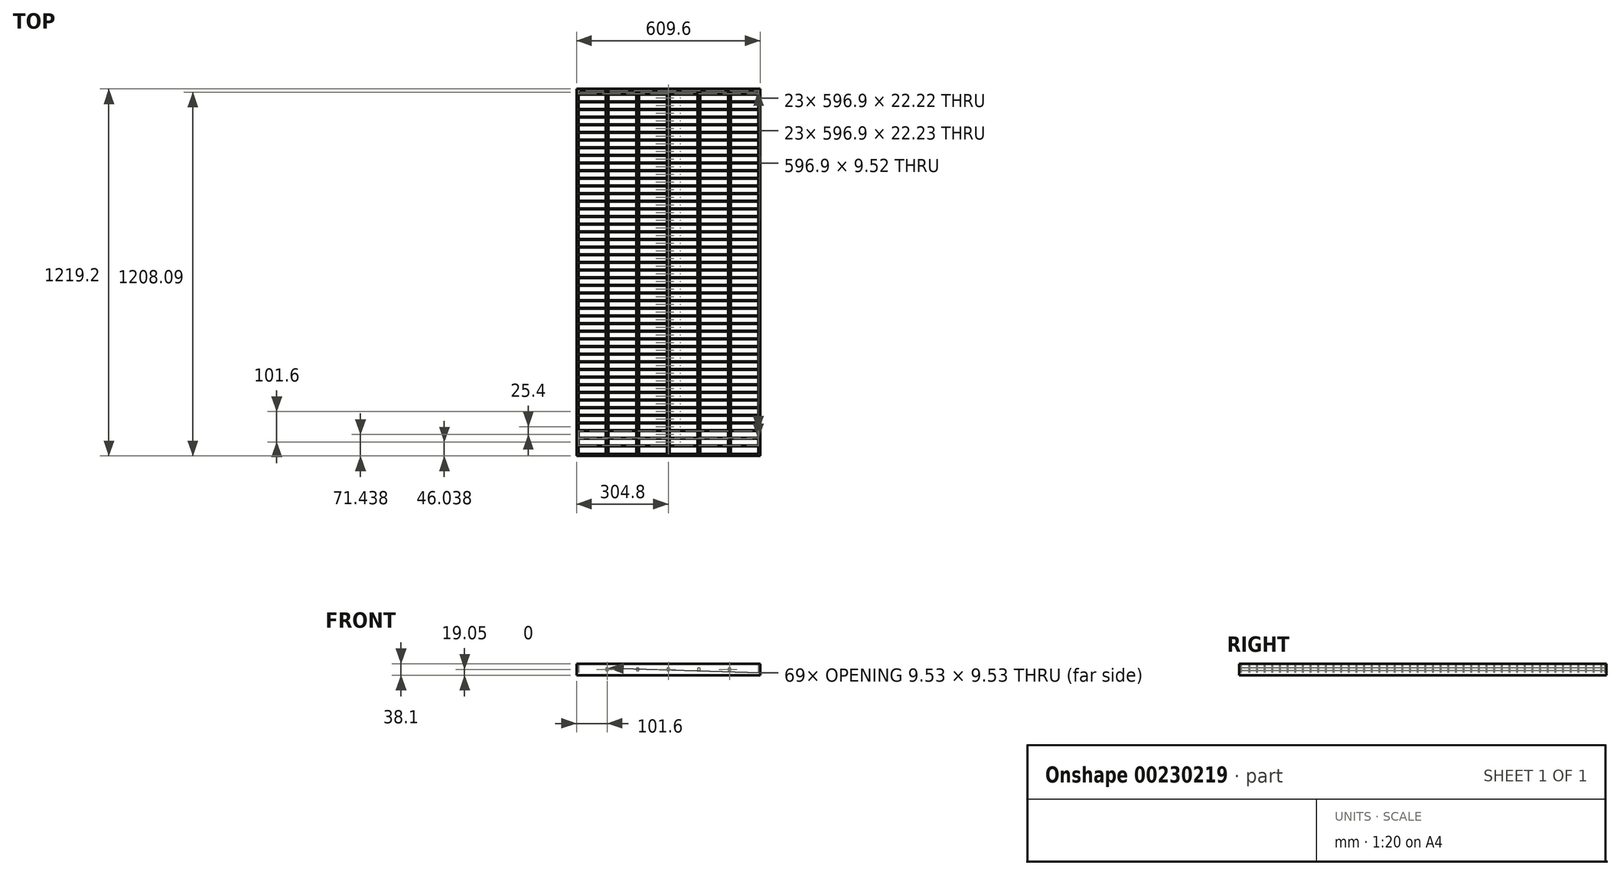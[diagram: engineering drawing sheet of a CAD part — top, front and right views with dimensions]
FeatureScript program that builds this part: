
annotation { "Feature Type Name" : "Feature", "Feature Type Description" : "" }
export const myFeature = defineFeature(function(context is Context, id is Id, definition is map)
    precondition{}
    {
        {
            var Q0;
            Q0=qCreatedBy(makeId("Top.planeOp"),FACE);
            var sketch = newSketch(context, id + "F0", { "sketchPlane" : qUnion([Q0])});
            skLineSegment(sketch, "E0.bottom", {"start": v(304.8, 609.6) * mm, "end": v(-304.8, 609.6) * mm});
            skLineSegment(sketch, "E0.top", {"start": v(304.8, -609.6) * mm, "end": v(-304.8, -609.6) * mm});
            skLineSegment(sketch, "E0.left", {"start": v(304.8, 609.6) * mm, "end": v(304.8, -609.6) * mm});
            skLineSegment(sketch, "E0.right", {"start": v(-304.8, 609.6) * mm, "end": v(-304.8, -609.6) * mm});
            skPoint(sketch, "E0.middle", {"position": v(0, 0) * mm});
            skLineSegment(sketch, "E1.bottom", {"start": v(-298.45, 603.25) * mm, "end": v(298.45, 603.25) * mm});
            skLineSegment(sketch, "E1.top", {"start": v(-298.45, -603.25) * mm, "end": v(298.45, -603.25) * mm});
            skLineSegment(sketch, "E1.left", {"start": v(-298.45, 603.25) * mm, "end": v(-298.45, -603.25) * mm});
            skLineSegment(sketch, "E1.right", {"start": v(298.45, 603.25) * mm, "end": v(298.45, -603.25) * mm});
            skLineSegment(sketch, "E2", {"start": v(-298.45, -603.25) * mm, "end": v(-298.45, -577.85) * mm});
            skLineSegment(sketch, "E3", {"start": v(-298.45, -577.85) * mm, "end": v(298.45, -577.85) * mm});
            skLineSegment(sketch, "E4", {"start": v(298.45, -577.85) * mm, "end": v(298.45, -574.67) * mm});
            skLineSegment(sketch, "E5", {"start": v(298.45, -574.67) * mm, "end": v(-298.45, -574.67) * mm});
            skLineSegment(sketch, "E6", {"start": v(-298.45, -574.67) * mm, "end": v(-298.45, -577.85) * mm});
            skLineSegment(sketch, "E7.0.1.0", {"start": v(-298.45, -552.45) * mm, "end": v(298.45, -552.45) * mm});
            skLineSegment(sketch, "E7.0.1.1", {"start": v(298.45, -549.27) * mm, "end": v(-298.45, -549.27) * mm});
            skLineSegment(sketch, "E7.0.1.2", {"start": v(298.45, -552.45) * mm, "end": v(298.45, -549.27) * mm});
            skLineSegment(sketch, "E7.0.1.3", {"start": v(-298.45, -549.27) * mm, "end": v(-298.45, -552.45) * mm});
            skLineSegment(sketch, "E7.0.2.0", {"start": v(-298.45, -527.05) * mm, "end": v(298.45, -527.05) * mm});
            skLineSegment(sketch, "E7.0.2.1", {"start": v(298.45, -523.88) * mm, "end": v(-298.45, -523.88) * mm});
            skLineSegment(sketch, "E7.0.2.2", {"start": v(298.45, -527.05) * mm, "end": v(298.45, -523.88) * mm});
            skLineSegment(sketch, "E7.0.2.3", {"start": v(-298.45, -523.88) * mm, "end": v(-298.45, -527.05) * mm});
            skLineSegment(sketch, "E7.0.3.0", {"start": v(-298.45, -501.65) * mm, "end": v(298.45, -501.65) * mm});
            skLineSegment(sketch, "E7.0.3.1", {"start": v(298.45, -498.48) * mm, "end": v(-298.45, -498.47) * mm});
            skLineSegment(sketch, "E7.0.3.2", {"start": v(298.45, -501.65) * mm, "end": v(298.45, -498.48) * mm});
            skLineSegment(sketch, "E7.0.3.3", {"start": v(-298.45, -498.48) * mm, "end": v(-298.45, -501.65) * mm});
            skLineSegment(sketch, "E7.0.4.0", {"start": v(-298.45, -476.25) * mm, "end": v(298.45, -476.25) * mm});
            skLineSegment(sketch, "E7.0.4.1", {"start": v(298.45, -473.08) * mm, "end": v(-298.45, -473.07) * mm});
            skLineSegment(sketch, "E7.0.4.2", {"start": v(298.45, -476.25) * mm, "end": v(298.45, -473.08) * mm});
            skLineSegment(sketch, "E7.0.4.3", {"start": v(-298.45, -473.08) * mm, "end": v(-298.45, -476.25) * mm});
            skLineSegment(sketch, "E7.0.5.0", {"start": v(-298.45, -450.85) * mm, "end": v(298.45, -450.85) * mm});
            skLineSegment(sketch, "E7.0.5.1", {"start": v(298.45, -447.68) * mm, "end": v(-298.45, -447.68) * mm});
            skLineSegment(sketch, "E7.0.5.2", {"start": v(298.45, -450.85) * mm, "end": v(298.45, -447.68) * mm});
            skLineSegment(sketch, "E7.0.5.3", {"start": v(-298.45, -447.68) * mm, "end": v(-298.45, -450.85) * mm});
            skLineSegment(sketch, "E7.0.6.0", {"start": v(-298.45, -425.45) * mm, "end": v(298.45, -425.45) * mm});
            skLineSegment(sketch, "E7.0.6.1", {"start": v(298.45, -422.28) * mm, "end": v(-298.45, -422.28) * mm});
            skLineSegment(sketch, "E7.0.6.2", {"start": v(298.45, -425.45) * mm, "end": v(298.45, -422.28) * mm});
            skLineSegment(sketch, "E7.0.6.3", {"start": v(-298.45, -422.28) * mm, "end": v(-298.45, -425.45) * mm});
            skLineSegment(sketch, "E7.0.7.0", {"start": v(-298.45, -400.05) * mm, "end": v(298.45, -400.05) * mm});
            skLineSegment(sketch, "E7.0.7.1", {"start": v(298.45, -396.88) * mm, "end": v(-298.45, -396.88) * mm});
            skLineSegment(sketch, "E7.0.7.2", {"start": v(298.45, -400.05) * mm, "end": v(298.45, -396.88) * mm});
            skLineSegment(sketch, "E7.0.7.3", {"start": v(-298.45, -396.88) * mm, "end": v(-298.45, -400.05) * mm});
            skLineSegment(sketch, "E7.0.8.0", {"start": v(-298.45, -374.65) * mm, "end": v(298.45, -374.65) * mm});
            skLineSegment(sketch, "E7.0.8.1", {"start": v(298.45, -371.48) * mm, "end": v(-298.45, -371.48) * mm});
            skLineSegment(sketch, "E7.0.8.2", {"start": v(298.45, -374.65) * mm, "end": v(298.45, -371.48) * mm});
            skLineSegment(sketch, "E7.0.8.3", {"start": v(-298.45, -371.48) * mm, "end": v(-298.45, -374.65) * mm});
            skLineSegment(sketch, "E7.0.9.0", {"start": v(-298.45, -349.25) * mm, "end": v(298.45, -349.25) * mm});
            skLineSegment(sketch, "E7.0.9.1", {"start": v(298.45, -346.08) * mm, "end": v(-298.45, -346.08) * mm});
            skLineSegment(sketch, "E7.0.9.2", {"start": v(298.45, -349.25) * mm, "end": v(298.45, -346.08) * mm});
            skLineSegment(sketch, "E7.0.9.3", {"start": v(-298.45, -346.08) * mm, "end": v(-298.45, -349.25) * mm});
            skLineSegment(sketch, "E7.0.10.0", {"start": v(-298.45, -323.85) * mm, "end": v(298.45, -323.85) * mm});
            skLineSegment(sketch, "E7.0.10.1", {"start": v(298.45, -320.68) * mm, "end": v(-298.45, -320.68) * mm});
            skLineSegment(sketch, "E7.0.10.2", {"start": v(298.45, -323.85) * mm, "end": v(298.45, -320.68) * mm});
            skLineSegment(sketch, "E7.0.10.3", {"start": v(-298.45, -320.68) * mm, "end": v(-298.45, -323.85) * mm});
            skLineSegment(sketch, "E7.0.11.0", {"start": v(-298.45, -298.45) * mm, "end": v(298.45, -298.45) * mm});
            skLineSegment(sketch, "E7.0.11.1", {"start": v(298.45, -295.28) * mm, "end": v(-298.45, -295.28) * mm});
            skLineSegment(sketch, "E7.0.11.2", {"start": v(298.45, -298.45) * mm, "end": v(298.45, -295.28) * mm});
            skLineSegment(sketch, "E7.0.11.3", {"start": v(-298.45, -295.28) * mm, "end": v(-298.45, -298.45) * mm});
            skLineSegment(sketch, "E7.0.12.0", {"start": v(-298.45, -273.05) * mm, "end": v(298.45, -273.05) * mm});
            skLineSegment(sketch, "E7.0.12.1", {"start": v(298.45, -269.88) * mm, "end": v(-298.45, -269.88) * mm});
            skLineSegment(sketch, "E7.0.12.2", {"start": v(298.45, -273.05) * mm, "end": v(298.45, -269.88) * mm});
            skLineSegment(sketch, "E7.0.12.3", {"start": v(-298.45, -269.88) * mm, "end": v(-298.45, -273.05) * mm});
            skLineSegment(sketch, "E7.0.13.0", {"start": v(-298.45, -247.65) * mm, "end": v(298.45, -247.65) * mm});
            skLineSegment(sketch, "E7.0.13.1", {"start": v(298.45, -244.48) * mm, "end": v(-298.45, -244.48) * mm});
            skLineSegment(sketch, "E7.0.13.2", {"start": v(298.45, -247.65) * mm, "end": v(298.45, -244.48) * mm});
            skLineSegment(sketch, "E7.0.13.3", {"start": v(-298.45, -244.48) * mm, "end": v(-298.45, -247.65) * mm});
            skLineSegment(sketch, "E7.0.14.0", {"start": v(-298.45, -222.25) * mm, "end": v(298.45, -222.25) * mm});
            skLineSegment(sketch, "E7.0.14.1", {"start": v(298.45, -219.08) * mm, "end": v(-298.45, -219.08) * mm});
            skLineSegment(sketch, "E7.0.14.2", {"start": v(298.45, -222.25) * mm, "end": v(298.45, -219.08) * mm});
            skLineSegment(sketch, "E7.0.14.3", {"start": v(-298.45, -219.08) * mm, "end": v(-298.45, -222.25) * mm});
            skLineSegment(sketch, "E7.0.15.0", {"start": v(-298.45, -196.85) * mm, "end": v(298.45, -196.85) * mm});
            skLineSegment(sketch, "E7.0.15.1", {"start": v(298.45, -193.68) * mm, "end": v(-298.45, -193.68) * mm});
            skLineSegment(sketch, "E7.0.15.2", {"start": v(298.45, -196.85) * mm, "end": v(298.45, -193.68) * mm});
            skLineSegment(sketch, "E7.0.15.3", {"start": v(-298.45, -193.68) * mm, "end": v(-298.45, -196.85) * mm});
            skLineSegment(sketch, "E7.0.16.0", {"start": v(-298.45, -171.45) * mm, "end": v(298.45, -171.45) * mm});
            skLineSegment(sketch, "E7.0.16.1", {"start": v(298.45, -168.28) * mm, "end": v(-298.45, -168.28) * mm});
            skLineSegment(sketch, "E7.0.16.2", {"start": v(298.45, -171.45) * mm, "end": v(298.45, -168.28) * mm});
            skLineSegment(sketch, "E7.0.16.3", {"start": v(-298.45, -168.28) * mm, "end": v(-298.45, -171.45) * mm});
            skLineSegment(sketch, "E7.0.17.0", {"start": v(-298.45, -146.05) * mm, "end": v(298.45, -146.05) * mm});
            skLineSegment(sketch, "E7.0.17.1", {"start": v(298.45, -142.88) * mm, "end": v(-298.45, -142.88) * mm});
            skLineSegment(sketch, "E7.0.17.2", {"start": v(298.45, -146.05) * mm, "end": v(298.45, -142.88) * mm});
            skLineSegment(sketch, "E7.0.17.3", {"start": v(-298.45, -142.88) * mm, "end": v(-298.45, -146.05) * mm});
            skLineSegment(sketch, "E7.0.18.0", {"start": v(-298.45, -120.65) * mm, "end": v(298.45, -120.65) * mm});
            skLineSegment(sketch, "E7.0.18.1", {"start": v(298.45, -117.48) * mm, "end": v(-298.45, -117.48) * mm});
            skLineSegment(sketch, "E7.0.18.2", {"start": v(298.45, -120.65) * mm, "end": v(298.45, -117.48) * mm});
            skLineSegment(sketch, "E7.0.18.3", {"start": v(-298.45, -117.48) * mm, "end": v(-298.45, -120.65) * mm});
            skLineSegment(sketch, "E7.0.19.0", {"start": v(-298.45, -95.25) * mm, "end": v(298.45, -95.25) * mm});
            skLineSegment(sketch, "E7.0.19.1", {"start": v(298.45, -92.08) * mm, "end": v(-298.45, -92.08) * mm});
            skLineSegment(sketch, "E7.0.19.2", {"start": v(298.45, -95.25) * mm, "end": v(298.45, -92.08) * mm});
            skLineSegment(sketch, "E7.0.19.3", {"start": v(-298.45, -92.08) * mm, "end": v(-298.45, -95.25) * mm});
            skLineSegment(sketch, "E7.0.20.0", {"start": v(-298.45, -69.85) * mm, "end": v(298.45, -69.85) * mm});
            skLineSegment(sketch, "E7.0.20.1", {"start": v(298.45, -66.68) * mm, "end": v(-298.45, -66.68) * mm});
            skLineSegment(sketch, "E7.0.20.2", {"start": v(298.45, -69.85) * mm, "end": v(298.45, -66.68) * mm});
            skLineSegment(sketch, "E7.0.20.3", {"start": v(-298.45, -66.68) * mm, "end": v(-298.45, -69.85) * mm});
            skLineSegment(sketch, "E7.0.21.0", {"start": v(-298.45, -44.45) * mm, "end": v(298.45, -44.45) * mm});
            skLineSegment(sketch, "E7.0.21.1", {"start": v(298.45, -41.28) * mm, "end": v(-298.45, -41.28) * mm});
            skLineSegment(sketch, "E7.0.21.2", {"start": v(298.45, -44.45) * mm, "end": v(298.45, -41.28) * mm});
            skLineSegment(sketch, "E7.0.21.3", {"start": v(-298.45, -41.28) * mm, "end": v(-298.45, -44.45) * mm});
            skLineSegment(sketch, "E7.0.22.0", {"start": v(-298.45, -19.05) * mm, "end": v(298.45, -19.05) * mm});
            skLineSegment(sketch, "E7.0.22.1", {"start": v(298.45, -15.88) * mm, "end": v(-298.45, -15.88) * mm});
            skLineSegment(sketch, "E7.0.22.2", {"start": v(298.45, -19.05) * mm, "end": v(298.45, -15.88) * mm});
            skLineSegment(sketch, "E7.0.22.3", {"start": v(-298.45, -15.88) * mm, "end": v(-298.45, -19.05) * mm});
            skLineSegment(sketch, "E7.0.23.0", {"start": v(-298.45, 6.35) * mm, "end": v(298.45, 6.35) * mm});
            skLineSegment(sketch, "E7.0.23.1", {"start": v(298.45, 9.52) * mm, "end": v(-298.45, 9.52) * mm});
            skLineSegment(sketch, "E7.0.23.2", {"start": v(298.45, 6.35) * mm, "end": v(298.45, 9.52) * mm});
            skLineSegment(sketch, "E7.0.23.3", {"start": v(-298.45, 9.52) * mm, "end": v(-298.45, 6.35) * mm});
            skLineSegment(sketch, "E7.0.24.0", {"start": v(-298.45, 31.75) * mm, "end": v(298.45, 31.75) * mm});
            skLineSegment(sketch, "E7.0.24.1", {"start": v(298.45, 34.92) * mm, "end": v(-298.45, 34.92) * mm});
            skLineSegment(sketch, "E7.0.24.2", {"start": v(298.45, 31.75) * mm, "end": v(298.45, 34.92) * mm});
            skLineSegment(sketch, "E7.0.24.3", {"start": v(-298.45, 34.92) * mm, "end": v(-298.45, 31.75) * mm});
            skLineSegment(sketch, "E7.0.25.0", {"start": v(-298.45, 57.15) * mm, "end": v(298.45, 57.15) * mm});
            skLineSegment(sketch, "E7.0.25.1", {"start": v(298.45, 60.32) * mm, "end": v(-298.45, 60.32) * mm});
            skLineSegment(sketch, "E7.0.25.2", {"start": v(298.45, 57.15) * mm, "end": v(298.45, 60.32) * mm});
            skLineSegment(sketch, "E7.0.25.3", {"start": v(-298.45, 60.32) * mm, "end": v(-298.45, 57.15) * mm});
            skLineSegment(sketch, "E7.0.26.0", {"start": v(-298.45, 82.55) * mm, "end": v(298.45, 82.55) * mm});
            skLineSegment(sketch, "E7.0.26.1", {"start": v(298.45, 85.72) * mm, "end": v(-298.45, 85.72) * mm});
            skLineSegment(sketch, "E7.0.26.2", {"start": v(298.45, 82.55) * mm, "end": v(298.45, 85.72) * mm});
            skLineSegment(sketch, "E7.0.26.3", {"start": v(-298.45, 85.72) * mm, "end": v(-298.45, 82.55) * mm});
            skLineSegment(sketch, "E7.0.27.0", {"start": v(-298.45, 107.95) * mm, "end": v(298.45, 107.95) * mm});
            skLineSegment(sketch, "E7.0.27.1", {"start": v(298.45, 111.12) * mm, "end": v(-298.45, 111.12) * mm});
            skLineSegment(sketch, "E7.0.27.2", {"start": v(298.45, 107.95) * mm, "end": v(298.45, 111.12) * mm});
            skLineSegment(sketch, "E7.0.27.3", {"start": v(-298.45, 111.12) * mm, "end": v(-298.45, 107.95) * mm});
            skLineSegment(sketch, "E7.0.28.0", {"start": v(-298.45, 133.35) * mm, "end": v(298.45, 133.35) * mm});
            skLineSegment(sketch, "E7.0.28.1", {"start": v(298.45, 136.52) * mm, "end": v(-298.45, 136.52) * mm});
            skLineSegment(sketch, "E7.0.28.2", {"start": v(298.45, 133.35) * mm, "end": v(298.45, 136.52) * mm});
            skLineSegment(sketch, "E7.0.28.3", {"start": v(-298.45, 136.52) * mm, "end": v(-298.45, 133.35) * mm});
            skLineSegment(sketch, "E7.0.29.0", {"start": v(-298.45, 158.75) * mm, "end": v(298.45, 158.75) * mm});
            skLineSegment(sketch, "E7.0.29.1", {"start": v(298.45, 161.92) * mm, "end": v(-298.45, 161.92) * mm});
            skLineSegment(sketch, "E7.0.29.2", {"start": v(298.45, 158.75) * mm, "end": v(298.45, 161.92) * mm});
            skLineSegment(sketch, "E7.0.29.3", {"start": v(-298.45, 161.92) * mm, "end": v(-298.45, 158.75) * mm});
            skLineSegment(sketch, "E7.0.30.0", {"start": v(-298.45, 184.15) * mm, "end": v(298.45, 184.15) * mm});
            skLineSegment(sketch, "E7.0.30.1", {"start": v(298.45, 187.32) * mm, "end": v(-298.45, 187.32) * mm});
            skLineSegment(sketch, "E7.0.30.2", {"start": v(298.45, 184.15) * mm, "end": v(298.45, 187.32) * mm});
            skLineSegment(sketch, "E7.0.30.3", {"start": v(-298.45, 187.32) * mm, "end": v(-298.45, 184.15) * mm});
            skLineSegment(sketch, "E7.0.31.0", {"start": v(-298.45, 209.55) * mm, "end": v(298.45, 209.55) * mm});
            skLineSegment(sketch, "E7.0.31.1", {"start": v(298.45, 212.72) * mm, "end": v(-298.45, 212.72) * mm});
            skLineSegment(sketch, "E7.0.31.2", {"start": v(298.45, 209.55) * mm, "end": v(298.45, 212.72) * mm});
            skLineSegment(sketch, "E7.0.31.3", {"start": v(-298.45, 212.72) * mm, "end": v(-298.45, 209.55) * mm});
            skLineSegment(sketch, "E7.0.32.0", {"start": v(-298.45, 234.95) * mm, "end": v(298.45, 234.95) * mm});
            skLineSegment(sketch, "E7.0.32.1", {"start": v(298.45, 238.12) * mm, "end": v(-298.45, 238.12) * mm});
            skLineSegment(sketch, "E7.0.32.2", {"start": v(298.45, 234.95) * mm, "end": v(298.45, 238.12) * mm});
            skLineSegment(sketch, "E7.0.32.3", {"start": v(-298.45, 238.12) * mm, "end": v(-298.45, 234.95) * mm});
            skLineSegment(sketch, "E7.0.33.0", {"start": v(-298.45, 260.35) * mm, "end": v(298.45, 260.35) * mm});
            skLineSegment(sketch, "E7.0.33.1", {"start": v(298.45, 263.52) * mm, "end": v(-298.45, 263.52) * mm});
            skLineSegment(sketch, "E7.0.33.2", {"start": v(298.45, 260.35) * mm, "end": v(298.45, 263.52) * mm});
            skLineSegment(sketch, "E7.0.33.3", {"start": v(-298.45, 263.52) * mm, "end": v(-298.45, 260.35) * mm});
            skLineSegment(sketch, "E7.0.34.0", {"start": v(-298.45, 285.75) * mm, "end": v(298.45, 285.75) * mm});
            skLineSegment(sketch, "E7.0.34.1", {"start": v(298.45, 288.92) * mm, "end": v(-298.45, 288.92) * mm});
            skLineSegment(sketch, "E7.0.34.2", {"start": v(298.45, 285.75) * mm, "end": v(298.45, 288.92) * mm});
            skLineSegment(sketch, "E7.0.34.3", {"start": v(-298.45, 288.92) * mm, "end": v(-298.45, 285.75) * mm});
            skLineSegment(sketch, "E7.0.35.0", {"start": v(-298.45, 311.15) * mm, "end": v(298.45, 311.15) * mm});
            skLineSegment(sketch, "E7.0.35.1", {"start": v(298.45, 314.32) * mm, "end": v(-298.45, 314.32) * mm});
            skLineSegment(sketch, "E7.0.35.2", {"start": v(298.45, 311.15) * mm, "end": v(298.45, 314.32) * mm});
            skLineSegment(sketch, "E7.0.35.3", {"start": v(-298.45, 314.32) * mm, "end": v(-298.45, 311.15) * mm});
            skLineSegment(sketch, "E7.0.36.0", {"start": v(-298.45, 336.55) * mm, "end": v(298.45, 336.55) * mm});
            skLineSegment(sketch, "E7.0.36.1", {"start": v(298.45, 339.72) * mm, "end": v(-298.45, 339.72) * mm});
            skLineSegment(sketch, "E7.0.36.2", {"start": v(298.45, 336.55) * mm, "end": v(298.45, 339.72) * mm});
            skLineSegment(sketch, "E7.0.36.3", {"start": v(-298.45, 339.72) * mm, "end": v(-298.45, 336.55) * mm});
            skLineSegment(sketch, "E7.0.37.0", {"start": v(-298.45, 361.95) * mm, "end": v(298.45, 361.95) * mm});
            skLineSegment(sketch, "E7.0.37.1", {"start": v(298.45, 365.12) * mm, "end": v(-298.45, 365.12) * mm});
            skLineSegment(sketch, "E7.0.37.2", {"start": v(298.45, 361.95) * mm, "end": v(298.45, 365.12) * mm});
            skLineSegment(sketch, "E7.0.37.3", {"start": v(-298.45, 365.12) * mm, "end": v(-298.45, 361.95) * mm});
            skLineSegment(sketch, "E7.0.38.0", {"start": v(-298.45, 387.35) * mm, "end": v(298.45, 387.35) * mm});
            skLineSegment(sketch, "E7.0.38.1", {"start": v(298.45, 390.52) * mm, "end": v(-298.45, 390.52) * mm});
            skLineSegment(sketch, "E7.0.38.2", {"start": v(298.45, 387.35) * mm, "end": v(298.45, 390.52) * mm});
            skLineSegment(sketch, "E7.0.38.3", {"start": v(-298.45, 390.52) * mm, "end": v(-298.45, 387.35) * mm});
            skLineSegment(sketch, "E7.0.39.0", {"start": v(-298.45, 412.75) * mm, "end": v(298.45, 412.75) * mm});
            skLineSegment(sketch, "E7.0.39.1", {"start": v(298.45, 415.92) * mm, "end": v(-298.45, 415.92) * mm});
            skLineSegment(sketch, "E7.0.39.2", {"start": v(298.45, 412.75) * mm, "end": v(298.45, 415.92) * mm});
            skLineSegment(sketch, "E7.0.39.3", {"start": v(-298.45, 415.92) * mm, "end": v(-298.45, 412.75) * mm});
            skLineSegment(sketch, "E7.0.40.0", {"start": v(-298.45, 438.15) * mm, "end": v(298.45, 438.15) * mm});
            skLineSegment(sketch, "E7.0.40.1", {"start": v(298.45, 441.32) * mm, "end": v(-298.45, 441.32) * mm});
            skLineSegment(sketch, "E7.0.40.2", {"start": v(298.45, 438.15) * mm, "end": v(298.45, 441.32) * mm});
            skLineSegment(sketch, "E7.0.40.3", {"start": v(-298.45, 441.32) * mm, "end": v(-298.45, 438.15) * mm});
            skLineSegment(sketch, "E7.0.41.0", {"start": v(-298.45, 463.55) * mm, "end": v(298.45, 463.55) * mm});
            skLineSegment(sketch, "E7.0.41.1", {"start": v(298.45, 466.72) * mm, "end": v(-298.45, 466.72) * mm});
            skLineSegment(sketch, "E7.0.41.2", {"start": v(298.45, 463.55) * mm, "end": v(298.45, 466.72) * mm});
            skLineSegment(sketch, "E7.0.41.3", {"start": v(-298.45, 466.72) * mm, "end": v(-298.45, 463.55) * mm});
            skLineSegment(sketch, "E7.0.42.0", {"start": v(-298.45, 488.95) * mm, "end": v(298.45, 488.95) * mm});
            skLineSegment(sketch, "E7.0.42.1", {"start": v(298.45, 492.12) * mm, "end": v(-298.45, 492.12) * mm});
            skLineSegment(sketch, "E7.0.42.2", {"start": v(298.45, 488.95) * mm, "end": v(298.45, 492.12) * mm});
            skLineSegment(sketch, "E7.0.42.3", {"start": v(-298.45, 492.12) * mm, "end": v(-298.45, 488.95) * mm});
            skLineSegment(sketch, "E7.0.43.0", {"start": v(-298.45, 514.35) * mm, "end": v(298.45, 514.35) * mm});
            skLineSegment(sketch, "E7.0.43.1", {"start": v(298.45, 517.52) * mm, "end": v(-298.45, 517.52) * mm});
            skLineSegment(sketch, "E7.0.43.2", {"start": v(298.45, 514.35) * mm, "end": v(298.45, 517.52) * mm});
            skLineSegment(sketch, "E7.0.43.3", {"start": v(-298.45, 517.52) * mm, "end": v(-298.45, 514.35) * mm});
            skLineSegment(sketch, "E7.0.44.0", {"start": v(-298.45, 539.75) * mm, "end": v(298.45, 539.75) * mm});
            skLineSegment(sketch, "E7.0.44.1", {"start": v(298.45, 542.92) * mm, "end": v(-298.45, 542.92) * mm});
            skLineSegment(sketch, "E7.0.44.2", {"start": v(298.45, 539.75) * mm, "end": v(298.45, 542.92) * mm});
            skLineSegment(sketch, "E7.0.44.3", {"start": v(-298.45, 542.92) * mm, "end": v(-298.45, 539.75) * mm});
            skLineSegment(sketch, "E7.0.45.0", {"start": v(-298.45, 565.15) * mm, "end": v(298.45, 565.15) * mm});
            skLineSegment(sketch, "E7.0.45.1", {"start": v(298.45, 568.32) * mm, "end": v(-298.45, 568.32) * mm});
            skLineSegment(sketch, "E7.0.45.2", {"start": v(298.45, 565.15) * mm, "end": v(298.45, 568.32) * mm});
            skLineSegment(sketch, "E7.0.45.3", {"start": v(-298.45, 568.32) * mm, "end": v(-298.45, 565.15) * mm});
            skLineSegment(sketch, "E7.0.46.0", {"start": v(-298.45, 590.55) * mm, "end": v(298.45, 590.55) * mm});
            skLineSegment(sketch, "E7.0.46.1", {"start": v(298.45, 593.72) * mm, "end": v(-298.45, 593.72) * mm});
            skLineSegment(sketch, "E7.0.46.2", {"start": v(298.45, 590.55) * mm, "end": v(298.45, 593.72) * mm});
            skLineSegment(sketch, "E7.0.46.3", {"start": v(-298.45, 593.72) * mm, "end": v(-298.45, 590.55) * mm});
            skLineSegment(sketch, "E7.direction1", {"start": v(-298.45, -577.85) * mm, "end": v(-273.05, -577.85) * mm, "construction": true});
            skLineSegment(sketch, "E7.direction2", {"start": v(-298.45, -577.85) * mm, "end": v(-298.45, -552.45) * mm, "construction": true});
            skSolve(sketch);
        }
        {
            var Q0;
            Q0 = qSketchRegion(id + "F0", true);
            var Q1;
            Q1=makeQuery(id+"F0.imprint","IMPRINT",FACE,{"disambiguationData":[TD([[makeQuery(id+"F0.imprint","IMPRINT",EDGE,{"derivedFrom":sQuery(id+"F0.wireOp",EDGE,"E3")}),1.0]])]});
            var Q2;
            Q2=makeQuery(id+"F0.imprint","IMPRINT",FACE,{"disambiguationData":[TD([[makeQuery(id+"F0.imprint","IMPRINT",EDGE,{"derivedFrom":sQuery(id+"F0.wireOp",EDGE,"E7.0.1.0")}),1.0]])]});
            var Q3;
            Q3=makeQuery(id+"F0.imprint","IMPRINT",FACE,{"disambiguationData":[TD([[makeQuery(id+"F0.imprint","IMPRINT",EDGE,{"derivedFrom":sQuery(id+"F0.wireOp",EDGE,"E7.0.2.0")}),1.0]])]});
            var Q4;
            Q4=makeQuery(id+"F0.imprint","IMPRINT",FACE,{"disambiguationData":[TD([[makeQuery(id+"F0.imprint","IMPRINT",EDGE,{"derivedFrom":sQuery(id+"F0.wireOp",EDGE,"E7.0.3.0")}),1.0]])]});
            var Q5;
            Q5=makeQuery(id+"F0.imprint","IMPRINT",FACE,{"disambiguationData":[TD([[makeQuery(id+"F0.imprint","IMPRINT",EDGE,{"derivedFrom":sQuery(id+"F0.wireOp",EDGE,"E7.0.4.0")}),1.0]])]});
            var Q6;
            Q6=makeQuery(id+"F0.imprint","IMPRINT",FACE,{"disambiguationData":[TD([[makeQuery(id+"F0.imprint","IMPRINT",EDGE,{"derivedFrom":sQuery(id+"F0.wireOp",EDGE,"E7.0.5.0")}),1.0]])]});
            var Q7;
            Q7=makeQuery(id+"F0.imprint","IMPRINT",FACE,{"disambiguationData":[TD([[makeQuery(id+"F0.imprint","IMPRINT",EDGE,{"derivedFrom":sQuery(id+"F0.wireOp",EDGE,"E7.0.6.0")}),1.0]])]});
            var Q8;
            Q8=makeQuery(id+"F0.imprint","IMPRINT",FACE,{"disambiguationData":[TD([[makeQuery(id+"F0.imprint","IMPRINT",EDGE,{"derivedFrom":sQuery(id+"F0.wireOp",EDGE,"E7.0.7.0")}),1.0]])]});
            var Q9;
            Q9=makeQuery(id+"F0.imprint","IMPRINT",FACE,{"disambiguationData":[TD([[makeQuery(id+"F0.imprint","IMPRINT",EDGE,{"derivedFrom":sQuery(id+"F0.wireOp",EDGE,"E7.0.8.0")}),1.0]])]});
            var Q10;
            Q10=makeQuery(id+"F0.imprint","IMPRINT",FACE,{"disambiguationData":[TD([[makeQuery(id+"F0.imprint","IMPRINT",EDGE,{"derivedFrom":sQuery(id+"F0.wireOp",EDGE,"E7.0.9.0")}),1.0]])]});
            var Q11;
            Q11=makeQuery(id+"F0.imprint","IMPRINT",FACE,{"disambiguationData":[TD([[makeQuery(id+"F0.imprint","IMPRINT",EDGE,{"derivedFrom":sQuery(id+"F0.wireOp",EDGE,"E7.0.10.0")}),1.0]])]});
            var Q12;
            Q12=makeQuery(id+"F0.imprint","IMPRINT",FACE,{"disambiguationData":[TD([[makeQuery(id+"F0.imprint","IMPRINT",EDGE,{"derivedFrom":sQuery(id+"F0.wireOp",EDGE,"E7.0.11.0")}),1.0]])]});
            var Q13;
            Q13=makeQuery(id+"F0.imprint","IMPRINT",FACE,{"disambiguationData":[TD([[makeQuery(id+"F0.imprint","IMPRINT",EDGE,{"derivedFrom":sQuery(id+"F0.wireOp",EDGE,"E7.0.12.0")}),1.0]])]});
            var Q14;
            Q14=makeQuery(id+"F0.imprint","IMPRINT",FACE,{"disambiguationData":[TD([[makeQuery(id+"F0.imprint","IMPRINT",EDGE,{"derivedFrom":sQuery(id+"F0.wireOp",EDGE,"E7.0.13.0")}),1.0]])]});
            var Q15;
            Q15=makeQuery(id+"F0.imprint","IMPRINT",FACE,{"disambiguationData":[TD([[makeQuery(id+"F0.imprint","IMPRINT",EDGE,{"derivedFrom":sQuery(id+"F0.wireOp",EDGE,"E7.0.14.0")}),1.0]])]});
            var Q16;
            Q16=makeQuery(id+"F0.imprint","IMPRINT",FACE,{"disambiguationData":[TD([[makeQuery(id+"F0.imprint","IMPRINT",EDGE,{"derivedFrom":sQuery(id+"F0.wireOp",EDGE,"E7.0.15.0")}),1.0]])]});
            var Q17;
            Q17=makeQuery(id+"F0.imprint","IMPRINT",FACE,{"disambiguationData":[TD([[makeQuery(id+"F0.imprint","IMPRINT",EDGE,{"derivedFrom":sQuery(id+"F0.wireOp",EDGE,"E7.0.16.0")}),1.0]])]});
            var Q18;
            Q18=makeQuery(id+"F0.imprint","IMPRINT",FACE,{"disambiguationData":[TD([[makeQuery(id+"F0.imprint","IMPRINT",EDGE,{"derivedFrom":sQuery(id+"F0.wireOp",EDGE,"E7.0.17.0")}),1.0]])]});
            var Q19;
            Q19=makeQuery(id+"F0.imprint","IMPRINT",FACE,{"disambiguationData":[TD([[makeQuery(id+"F0.imprint","IMPRINT",EDGE,{"derivedFrom":sQuery(id+"F0.wireOp",EDGE,"E7.0.18.0")}),1.0]])]});
            var Q20;
            Q20=makeQuery(id+"F0.imprint","IMPRINT",FACE,{"disambiguationData":[TD([[makeQuery(id+"F0.imprint","IMPRINT",EDGE,{"derivedFrom":sQuery(id+"F0.wireOp",EDGE,"E7.0.19.0")}),1.0]])]});
            var Q21;
            Q21=makeQuery(id+"F0.imprint","IMPRINT",FACE,{"disambiguationData":[TD([[makeQuery(id+"F0.imprint","IMPRINT",EDGE,{"derivedFrom":sQuery(id+"F0.wireOp",EDGE,"E7.0.20.0")}),1.0]])]});
            var Q22;
            Q22=makeQuery(id+"F0.imprint","IMPRINT",FACE,{"disambiguationData":[TD([[makeQuery(id+"F0.imprint","IMPRINT",EDGE,{"derivedFrom":sQuery(id+"F0.wireOp",EDGE,"E7.0.21.0")}),1.0]])]});
            var Q23;
            Q23=makeQuery(id+"F0.imprint","IMPRINT",FACE,{"disambiguationData":[TD([[makeQuery(id+"F0.imprint","IMPRINT",EDGE,{"derivedFrom":sQuery(id+"F0.wireOp",EDGE,"E7.0.22.0")}),1.0]])]});
            var Q24;
            Q24=makeQuery(id+"F0.imprint","IMPRINT",FACE,{"disambiguationData":[TD([[makeQuery(id+"F0.imprint","IMPRINT",EDGE,{"derivedFrom":sQuery(id+"F0.wireOp",EDGE,"E7.0.23.0")}),1.0]])]});
            var Q25;
            Q25=makeQuery(id+"F0.imprint","IMPRINT",FACE,{"disambiguationData":[TD([[makeQuery(id+"F0.imprint","IMPRINT",EDGE,{"derivedFrom":sQuery(id+"F0.wireOp",EDGE,"E7.0.24.0")}),1.0]])]});
            var Q26;
            Q26=makeQuery(id+"F0.imprint","IMPRINT",FACE,{"disambiguationData":[TD([[makeQuery(id+"F0.imprint","IMPRINT",EDGE,{"derivedFrom":sQuery(id+"F0.wireOp",EDGE,"E7.0.25.0")}),1.0]])]});
            var Q27;
            Q27=makeQuery(id+"F0.imprint","IMPRINT",FACE,{"disambiguationData":[TD([[makeQuery(id+"F0.imprint","IMPRINT",EDGE,{"derivedFrom":sQuery(id+"F0.wireOp",EDGE,"E7.0.26.0")}),1.0]])]});
            var Q28;
            Q28=makeQuery(id+"F0.imprint","IMPRINT",FACE,{"disambiguationData":[TD([[makeQuery(id+"F0.imprint","IMPRINT",EDGE,{"derivedFrom":sQuery(id+"F0.wireOp",EDGE,"E7.0.27.0")}),1.0]])]});
            var Q29;
            Q29=makeQuery(id+"F0.imprint","IMPRINT",FACE,{"disambiguationData":[TD([[makeQuery(id+"F0.imprint","IMPRINT",EDGE,{"derivedFrom":sQuery(id+"F0.wireOp",EDGE,"E7.0.28.0")}),1.0]])]});
            var Q30;
            Q30=makeQuery(id+"F0.imprint","IMPRINT",FACE,{"disambiguationData":[TD([[makeQuery(id+"F0.imprint","IMPRINT",EDGE,{"derivedFrom":sQuery(id+"F0.wireOp",EDGE,"E7.0.29.0")}),1.0]])]});
            var Q31;
            Q31=makeQuery(id+"F0.imprint","IMPRINT",FACE,{"disambiguationData":[TD([[makeQuery(id+"F0.imprint","IMPRINT",EDGE,{"derivedFrom":sQuery(id+"F0.wireOp",EDGE,"E7.0.30.0")}),1.0]])]});
            var Q32;
            Q32=makeQuery(id+"F0.imprint","IMPRINT",FACE,{"disambiguationData":[TD([[makeQuery(id+"F0.imprint","IMPRINT",EDGE,{"derivedFrom":sQuery(id+"F0.wireOp",EDGE,"E7.0.31.0")}),1.0]])]});
            var Q33;
            Q33=makeQuery(id+"F0.imprint","IMPRINT",FACE,{"disambiguationData":[TD([[makeQuery(id+"F0.imprint","IMPRINT",EDGE,{"derivedFrom":sQuery(id+"F0.wireOp",EDGE,"E7.0.32.0")}),1.0]])]});
            var Q34;
            Q34=makeQuery(id+"F0.imprint","IMPRINT",FACE,{"disambiguationData":[TD([[makeQuery(id+"F0.imprint","IMPRINT",EDGE,{"derivedFrom":sQuery(id+"F0.wireOp",EDGE,"E7.0.33.0")}),1.0]])]});
            var Q35;
            Q35=makeQuery(id+"F0.imprint","IMPRINT",FACE,{"disambiguationData":[TD([[makeQuery(id+"F0.imprint","IMPRINT",EDGE,{"derivedFrom":sQuery(id+"F0.wireOp",EDGE,"E7.0.34.0")}),1.0]])]});
            var Q36;
            Q36=makeQuery(id+"F0.imprint","IMPRINT",FACE,{"disambiguationData":[TD([[makeQuery(id+"F0.imprint","IMPRINT",EDGE,{"derivedFrom":sQuery(id+"F0.wireOp",EDGE,"E7.0.35.0")}),1.0]])]});
            var Q37;
            Q37=makeQuery(id+"F0.imprint","IMPRINT",FACE,{"disambiguationData":[TD([[makeQuery(id+"F0.imprint","IMPRINT",EDGE,{"derivedFrom":sQuery(id+"F0.wireOp",EDGE,"E7.0.36.0")}),1.0]])]});
            var Q38;
            Q38=makeQuery(id+"F0.imprint","IMPRINT",FACE,{"disambiguationData":[TD([[makeQuery(id+"F0.imprint","IMPRINT",EDGE,{"derivedFrom":sQuery(id+"F0.wireOp",EDGE,"E7.0.37.0")}),1.0]])]});
            var Q39;
            Q39=makeQuery(id+"F0.imprint","IMPRINT",FACE,{"disambiguationData":[TD([[makeQuery(id+"F0.imprint","IMPRINT",EDGE,{"derivedFrom":sQuery(id+"F0.wireOp",EDGE,"E7.0.38.0")}),1.0]])]});
            var Q40;
            Q40=makeQuery(id+"F0.imprint","IMPRINT",FACE,{"disambiguationData":[TD([[makeQuery(id+"F0.imprint","IMPRINT",EDGE,{"derivedFrom":sQuery(id+"F0.wireOp",EDGE,"E7.0.39.0")}),1.0]])]});
            var Q41;
            Q41=makeQuery(id+"F0.imprint","IMPRINT",FACE,{"disambiguationData":[TD([[makeQuery(id+"F0.imprint","IMPRINT",EDGE,{"derivedFrom":sQuery(id+"F0.wireOp",EDGE,"E7.0.40.0")}),1.0]])]});
            var Q42;
            Q42=makeQuery(id+"F0.imprint","IMPRINT",FACE,{"disambiguationData":[TD([[makeQuery(id+"F0.imprint","IMPRINT",EDGE,{"derivedFrom":sQuery(id+"F0.wireOp",EDGE,"E7.0.41.0")}),1.0]])]});
            var Q43;
            Q43=makeQuery(id+"F0.imprint","IMPRINT",FACE,{"disambiguationData":[TD([[makeQuery(id+"F0.imprint","IMPRINT",EDGE,{"derivedFrom":sQuery(id+"F0.wireOp",EDGE,"E7.0.42.0")}),1.0]])]});
            var Q44;
            Q44=makeQuery(id+"F0.imprint","IMPRINT",FACE,{"disambiguationData":[TD([[makeQuery(id+"F0.imprint","IMPRINT",EDGE,{"derivedFrom":sQuery(id+"F0.wireOp",EDGE,"E7.0.43.0")}),1.0]])]});
            var Q45;
            Q45=makeQuery(id+"F0.imprint","IMPRINT",FACE,{"disambiguationData":[TD([[makeQuery(id+"F0.imprint","IMPRINT",EDGE,{"derivedFrom":sQuery(id+"F0.wireOp",EDGE,"E7.0.44.0")}),1.0]])]});
            var Q46;
            Q46=makeQuery(id+"F0.imprint","IMPRINT",FACE,{"disambiguationData":[TD([[makeQuery(id+"F0.imprint","IMPRINT",EDGE,{"derivedFrom":sQuery(id+"F0.wireOp",EDGE,"E7.0.45.0")}),1.0]])]});
            var Q47;
            Q47=makeQuery(id+"F0.imprint","IMPRINT",FACE,{"disambiguationData":[TD([[makeQuery(id+"F0.imprint","IMPRINT",EDGE,{"derivedFrom":sQuery(id+"F0.wireOp",EDGE,"E7.0.46.0")}),1.0]])]});
            extrude(context, id + "F1", {"entities" : qUnion([Q0, Q1, Q2, Q3, Q4, Q5, Q6, Q7, Q8, Q9, Q10, Q11, Q12, Q13, Q14, Q15, Q16, Q17, Q18, Q19, Q20, Q21, Q22, Q23, Q24, Q25, Q26, Q27, Q28, Q29, Q30, Q31, Q32, Q33, Q34, Q35, Q36, Q37, Q38, Q39, Q40, Q41, Q42, Q43, Q44, Q45, Q46, Q47]), "depth" : 38.1 * mm});
        }
        {
            var Q0;
            Q0=makeQuery(id+"F1.opExtrude","SWEPT_FACE",FACE,{"disambiguationData":[OSD([sQuery(id+"F0.wireOp",EDGE,"E0.top")])]});
            var sketch = newSketch(context, id + "F2", { "sketchPlane" : qUnion([Q0])});
            skLineSegment(sketch, "E8", {"start": v(-304.8, 19.05) * mm, "end": v(-203.2, 19.05) * mm});
            skLineSegment(sketch, "E9", {"start": v(-203.2, 19.05) * mm, "end": v(-101.6, 19.05) * mm});
            skLineSegment(sketch, "E10", {"start": v(-101.6, 19.05) * mm, "end": v(0, 19.05) * mm});
            skLineSegment(sketch, "E11", {"start": v(0, 19.05) * mm, "end": v(101.6, 19.05) * mm});
            skLineSegment(sketch, "E12", {"start": v(101.6, 19.05) * mm, "end": v(203.2, 19.05) * mm});
            skCircle(sketch, "E13", {"center": v(-203.2, 19.05) * mm, "radius": 4.76 * mm});
            skCircle(sketch, "E14", {"center": v(-101.6, 19.05) * mm, "radius": 4.76 * mm});
            skCircle(sketch, "E15", {"center": v(0, 19.05) * mm, "radius": 4.76 * mm});
            skCircle(sketch, "E16", {"center": v(101.6, 19.05) * mm, "radius": 4.76 * mm});
            skCircle(sketch, "E17", {"center": v(203.2, 19.05) * mm, "radius": 4.76 * mm});
            skSolve(sketch);
        }
        {
            var Q0;
            Q0 = qSketchRegion(id + "F2", true);
            extrude(context, id + "F3", {"entities" : qUnion([Q0]), "operationType" : NewBodyOperationType.ADD, "oppositeDirection" : true, "depth" : 1219.2 * mm});
        }
    });
